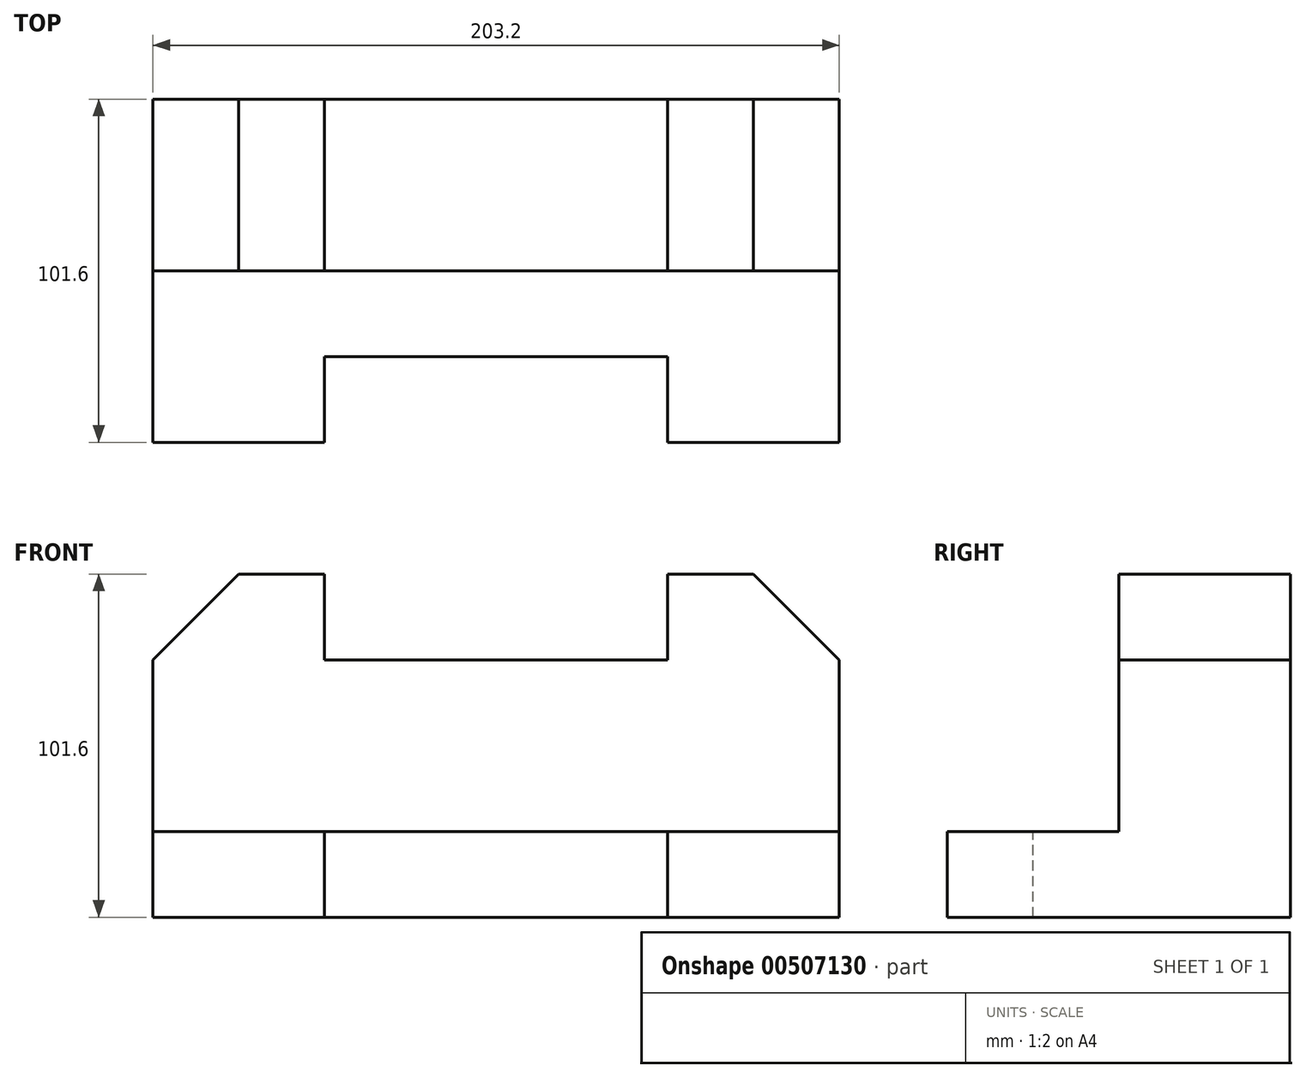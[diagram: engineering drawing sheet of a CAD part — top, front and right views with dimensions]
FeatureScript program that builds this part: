
annotation { "Feature Type Name" : "Feature", "Feature Type Description" : "" }
export const myFeature = defineFeature(function(context is Context, id is Id, definition is map)
    precondition{}
    {
        {
            var Q0;
            Q0=qCreatedBy(makeId("Front.planeOp"),FACE);
            var sketch = newSketch(context, id + "F0", { "sketchPlane" : qUnion([Q0])});
            skLineSegment(sketch, "E0.bottom", {"start": v(-104.28, 24.64) * mm, "end": v(-53.48, 24.64) * mm});
            skLineSegment(sketch, "E0.top", {"start": v(-104.28, -76.96) * mm, "end": v(98.92, -76.96) * mm});
            skLineSegment(sketch, "E0.left", {"start": v(-104.28, 24.64) * mm, "end": v(-104.28, -76.96) * mm});
            skLineSegment(sketch, "E0.right", {"start": v(98.92, 24.64) * mm, "end": v(98.92, -76.96) * mm});
            skLineSegment(sketch, "E1.top", {"start": v(-53.48, -0.76) * mm, "end": v(48.12, -0.76) * mm});
            skLineSegment(sketch, "E1.left", {"start": v(-53.48, 24.64) * mm, "end": v(-53.48, -0.76) * mm});
            skLineSegment(sketch, "E1.right", {"start": v(48.12, 24.64) * mm, "end": v(48.12, -0.76) * mm});
            skLineSegment(sketch, "E2.trimOffspring", {"start": v(48.12, 24.64) * mm, "end": v(98.92, 24.64) * mm});
            skSolve(sketch);
        }
        {
            var Q0;
            Q0 = qSketchRegion(id + "F0", true);
            extrude(context, id + "F1", {"entities" : qUnion([Q0]), "oppositeDirection" : true, "depth" : 101.6 * mm});
        }
        {
            var Q0;
            Q0=qCreatedBy(makeId("Front.planeOp"),FACE);
            var sketch = newSketch(context, id + "F2", { "sketchPlane" : qUnion([Q0])});
            skLineSegment(sketch, "E3.bottom", {"start": v(-104.28, 24.64) * mm, "end": v(98.92, 24.64) * mm});
            skLineSegment(sketch, "E3.top", {"start": v(-104.28, -51.56) * mm, "end": v(98.92, -51.56) * mm});
            skLineSegment(sketch, "E3.left", {"start": v(-104.28, 24.64) * mm, "end": v(-104.28, -51.56) * mm});
            skLineSegment(sketch, "E3.right", {"start": v(98.92, 24.64) * mm, "end": v(98.92, -51.56) * mm});
            skSolve(sketch);
        }
        {
            var Q0;
            Q0 = qSketchRegion(id + "F2", true);
            extrude(context, id + "F3", {"entities" : qUnion([Q0]), "operationType" : NewBodyOperationType.REMOVE, "oppositeDirection" : true, "depth" : 50.8 * mm});
        }
        {
            var Q0;
            Q0=qCreatedBy(makeId("Top.planeOp"),FACE);
            var sketch = newSketch(context, id + "F4", { "sketchPlane" : qUnion([Q0])});
            skLineSegment(sketch, "E4.bottom", {"start": v(-53.48, 0) * mm, "end": v(48.12, 0) * mm});
            skLineSegment(sketch, "E4.top", {"start": v(-53.48, 25.4) * mm, "end": v(48.12, 25.4) * mm});
            skLineSegment(sketch, "E4.left", {"start": v(-53.48, 0) * mm, "end": v(-53.48, 25.4) * mm});
            skLineSegment(sketch, "E4.right", {"start": v(48.12, 0) * mm, "end": v(48.12, 25.4) * mm});
            skSolve(sketch);
        }
        {
            var Q0;
            Q0=makeQuery(id+"F4.imprint","IMPRINT",FACE,{"disambiguationData":[TD([[makeQuery(id+"F4.imprint","IMPRINT",EDGE,{"derivedFrom":sQuery(id+"F4.wireOp",EDGE,"E4.bottom")}),1.0]])]});
            extrude(context, id + "F5", {"entities" : qUnion([Q0]), "operationType" : NewBodyOperationType.REMOVE, "endBound" : BoundingType.THROUGH_ALL, "oppositeDirection" : true, "depth" : 101.6 * mm});
        }
        {
            var Q0;
            Q0=makeQuery(id+"F1.opExtrude","SWEPT_EDGE",EDGE,{"disambiguationData":[OSD([sQuery(id+"F0.wireOp",EDGE,"E0.right"),sQuery(id+"F0.wireOp",EDGE,"E2.trimOffspring")])]});
            chamfer(context, id + "F6", {"entities" : qUnion([Q0]), "width" : 25.4 * mm, "tangentPropagation" : true});
        }
        {
            var Q0;
            Q0=makeQuery(id+"F1.opExtrude","SWEPT_EDGE",EDGE,{"disambiguationData":[OSD([sQuery(id+"F0.wireOp",EDGE,"E0.bottom"),sQuery(id+"F0.wireOp",EDGE,"E0.left")])]});
            chamfer(context, id + "F7", {"entities" : qUnion([Q0]), "width" : 25.4 * mm, "tangentPropagation" : true});
        }
    });
